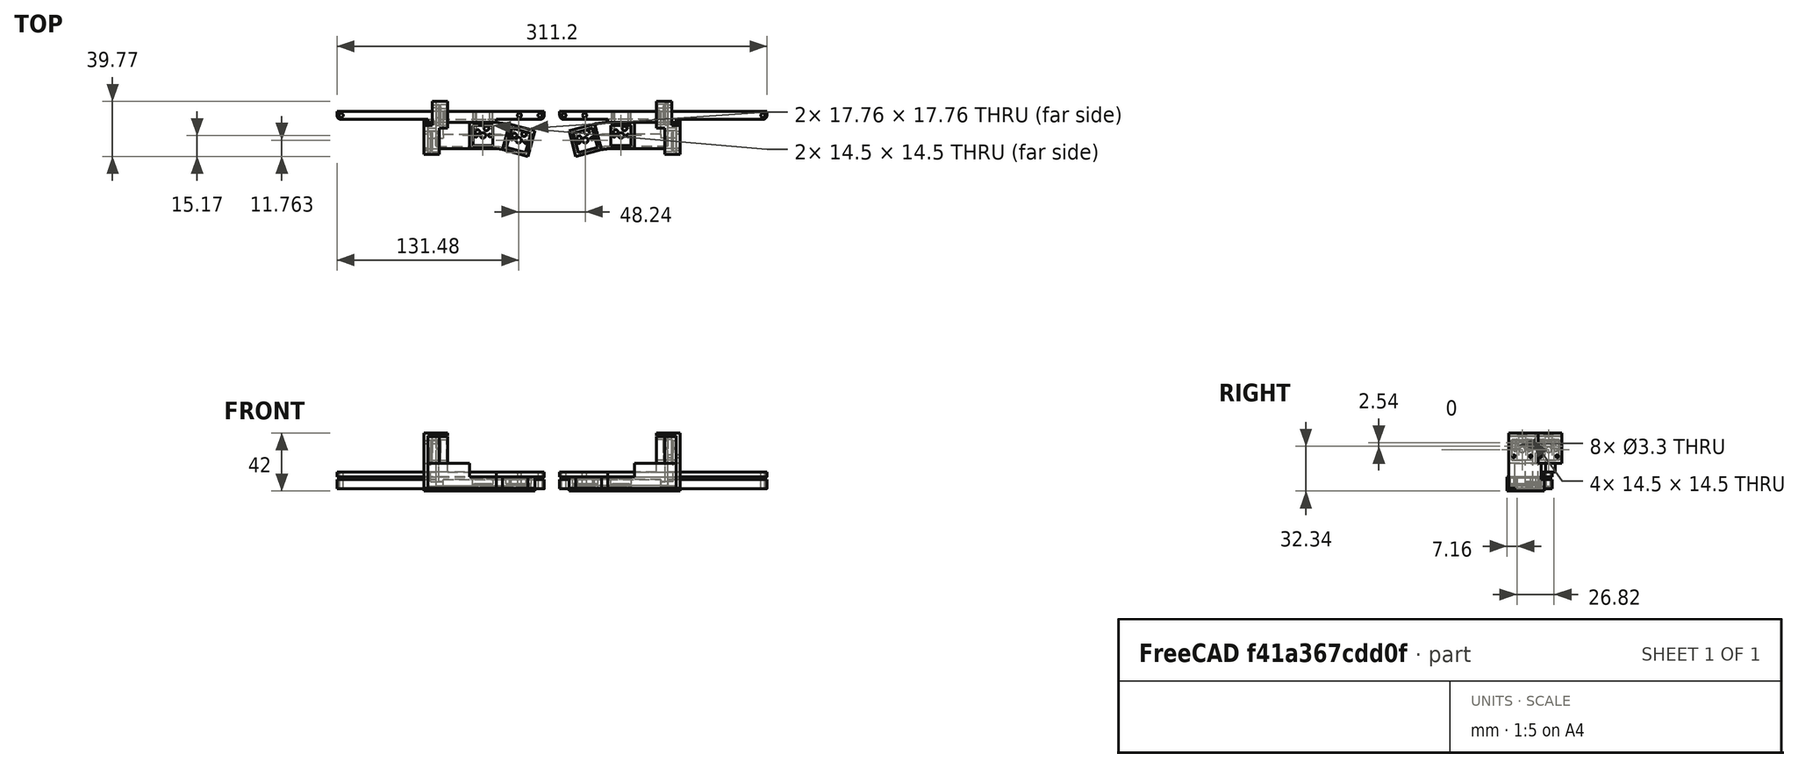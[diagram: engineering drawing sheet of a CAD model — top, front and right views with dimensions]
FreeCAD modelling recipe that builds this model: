
FCSTD DOCUMENT  (FreeCAD 0.21R33771 (Git))
Label: thumb_v2
License: All rights reserved
LicenseURL: https://en.wikipedia.org/wiki/All_rights_reserved
objects: Part::Box×23, Part::FeaturePython×21, Part::MultiFuse×20, Part::Part2DObjectPython×16, Part::Extrusion×16, Part::Cylinder×14, Part::Cut×11, Part::Fillet×2, Spreadsheet::Sheet×1
note: 123 computed .brp shape members not serialized (recipe doc carries the construction recipe); baked Part::Feature solids carry a one-line shape summary decoded from their .brp

FEATURE [Part::Box] Box  label="Cube"
  AttacherType = Attacher::AttachEngine3D
  Height = 8.2
  Length = 19.2
  Placement = pos=(-9.6,-9.6,-3.2) rot=(0,0,1;0rad)
  Width = 19.2
  expr: .Placement.Base.x = -<<CMX_Socket>>.s1 / 2
  expr: .Placement.Base.y = -<<CMX_Socket>>.s1 / 2
  expr: Length = <<CMX_Socket>>.s1
  expr: Width = <<CMX_Socket>>.s1
FEATURE [Part::Part2DObjectPython] Circle  # Draft 2D object (typed FeaturePython)
  Area = 12.5664
  FirstAngle = 0
  LastAngle = 0
  MakeFace = true
  Radius = 2
  expr: Radius = <<CMX_Socket>>.r1
FEATURE [Part::Part2DObjectPython] Circle001  # Draft 2D object (typed FeaturePython)
  Area = 4.15476
  FirstAngle = 0
  LastAngle = 0
  MakeFace = true
  Placement = pos=(-5.08,-2e-16,0) rot=(0,0,1;0rad)
  Radius = 1.15
  expr: .Placement.Base.x = -<<CMX_Socket>>.xr
  expr: Radius = <<CMX_Socket>>.r3
FEATURE [Part::Part2DObjectPython] Circle002  # Draft 2D object (typed FeaturePython)
  Area = 3.14159
  FirstAngle = 0
  LastAngle = 0
  MakeFace = true
  Placement = pos=(5.08,-2e-16,0) rot=(0,0,1;0rad)
  Radius = 1
  expr: .Placement.Base.x = <<CMX_Socket>>.xr
FEATURE [Part::Part2DObjectPython] Circle003  # Draft 2D object (typed FeaturePython)
  Area = 8.55299
  FirstAngle = 0
  LastAngle = 0
  MakeFace = true
  Placement = pos=(2.54,5.08,0) rot=(0,0,1;0rad)
  Radius = 1.65
  expr: .Placement.Base.x = <<CMX_Socket>>.x1
  expr: .Placement.Base.y = <<CMX_Socket>>.y1
  expr: Radius = <<CMX_Socket>>.r2
FEATURE [Part::Part2DObjectPython] Circle004  # Draft 2D object (typed FeaturePython)
  Area = 8.55299
  FirstAngle = 0
  LastAngle = 0
  MakeFace = true
  Placement = pos=(-3.81,2.54,0) rot=(0,0,1;0rad)
  Radius = 1.65
  expr: .Placement.Base.x = <<CMX_Socket>>.x2
  expr: .Placement.Base.y = <<CMX_Socket>>.y2
  expr: Radius = <<CMX_Socket>>.r2
FEATURE [Part::Extrusion] Extrude002
  Base = -> Circle
  Dir = (0,0,1)
  DirMode = 2
  FaceMakerClass = Part::FaceMakerBullseye
  LengthFwd = -3.2
  LengthRev = 0
  Solid = false
  Symmetric = false
  expr: LengthFwd = -<<CMX_Socket>>.h1 - <<CMX_Socket>>.h2
FEATURE [Part::Extrusion] Extrude003
  Base = -> Circle001
  Dir = (0,0,1)
  DirMode = 2
  FaceMakerClass = Part::FaceMakerBullseye
  LengthFwd = -3.2
  LengthRev = 0
  Solid = false
  Symmetric = false
  expr: LengthFwd = -<<CMX_Socket>>.h1 - <<CMX_Socket>>.h2
FEATURE [Part::Extrusion] Extrude004
  Base = -> Circle002
  Dir = (0,0,1)
  DirMode = 2
  FaceMakerClass = Part::FaceMakerBullseye
  LengthFwd = -3.2
  LengthRev = 0
  Solid = false
  Symmetric = false
  expr: LengthFwd = -<<CMX_Socket>>.h1 - <<CMX_Socket>>.h2
FEATURE [Part::Extrusion] Extrude005
  Base = -> Circle003
  Dir = (0,0,1)
  DirMode = 2
  FaceMakerClass = Part::FaceMakerBullseye
  LengthFwd = -1
  LengthRev = 0
  Solid = false
  Symmetric = false
  expr: LengthFwd = -<<CMX_Socket>>.h2
FEATURE [Part::Extrusion] Extrude006
  Base = -> Circle004
  Dir = (0,0,1)
  DirMode = 2
  FaceMakerClass = Part::FaceMakerBullseye
  LengthFwd = -1
  LengthRev = 0
  Solid = false
  Symmetric = false
  expr: LengthFwd = -<<CMX_Socket>>.h2
FEATURE [Part::Part2DObjectPython] Rectangle  # Draft 2D object (typed FeaturePython)
  Area = 90.6
  ChamferSize = 0
  Columns = 1
  FilletRadius = 0
  Height = 6
  Length = 15.1
  MakeFace = true
  Placement = pos=(-8.03,0.8,-1) rot=(0,0,1;0rad)
  Rows = 1
  expr: .Placement.Base.x = <<CMX_Socket>>.xl
  expr: .Placement.Base.y = <<CMX_Socket>>.yl
  expr: .Placement.Base.z = -<<CMX_Socket>>.h2
  expr: Height = <<CMX_Socket>>.ll
  expr: Length = <<CMX_Socket>>.wl
FEATURE [Part::Extrusion] Extrude007
  Base = -> Rectangle
  Dir = (0,0,1)
  DirMode = 2
  FaceMakerClass = Part::FaceMakerBullseye
  LengthFwd = -2.2
  LengthRev = 0
  Solid = false
  Symmetric = false
  expr: LengthFwd = -<<CMX_Socket>>.h1
FEATURE [Part::Part2DObjectPython] Rectangle001  # Draft 2D object (typed FeaturePython)
  Area = 225
  ChamferSize = 0
  Columns = 1
  FilletRadius = 0
  Height = 15
  Length = 15
  MakeFace = true
  Placement = pos=(-7.5,-7.5,0) rot=(0,0,1;0rad)
  Rows = 1
  expr: .Placement.Base.x = -<<CMX_Socket>>.s2 / 2
  expr: .Placement.Base.y = -<<CMX_Socket>>.s2 / 2
  expr: Height = <<CMX_Socket>>.s2
  expr: Length = <<CMX_Socket>>.s2
FEATURE [Part::Extrusion] Extrude001
  Base = -> Rectangle001
  Dir = (0,0,1)
  DirMode = 2
  FaceMakerClass = Part::FaceMakerBullseye
  LengthFwd = 4.5
  LengthRev = 0
  Solid = false
  Symmetric = false
  expr: LengthFwd = <<CMX_Socket>>.h3
FEATURE [Part::Part2DObjectPython] Rectangle002  # Draft 2D object (typed FeaturePython)
  Area = 210.25
  ChamferSize = 0
  Columns = 1
  FilletRadius = 0
  Height = 14.5
  Length = 14.5
  MakeFace = true
  Placement = pos=(-7.25,-7.25,4) rot=(0,0,1;0rad)
  Rows = 1
  expr: .Placement.Base.x = -<<CMX_Socket>>.s3 / 2
  expr: .Placement.Base.y = -<<CMX_Socket>>.s3 / 2
  expr: Height = <<CMX_Socket>>.s3
  expr: Length = <<CMX_Socket>>.s3
FEATURE [Part::Extrusion] Extrude
  Base = -> Rectangle002
  Dir = (0,0,1)
  DirMode = 2
  FaceMakerClass = Part::FaceMakerBullseye
  LengthFwd = 1.1
  LengthRev = 0
  Solid = false
  Symmetric = false
FEATURE [Part::MultiFuse] Fusion
  Shapes = -> [Extrude001,Extrude002,Extrude003,Extrude004,Extrude005,Extrude006,Extrude007,Extrude]
FEATURE [Part::Cut] Cut
  Base = -> Box
  Tool = -> Fusion
FEATURE [Spreadsheet::Sheet] Spreadsheet  label="CMX_Socket"
  cells = B3='r1; C3(r1)=2; D3='x1; E3(x1)=2.54; F3='y1; G3(y1)=5.08; B4='r2; C4(r2)=1.65; D4='x2; E4(x2)=-3.81; F4='y2; G4(y2)=2.54; B5='r3; C5(r3)=1.15; D5='xr; E5(xr)=5.08; B7='wl; C7(wl)=15.1; D7='xl; E7(xl)=-8.03; B8='ll; C8(ll)=6; D8='yl; E8(yl)=0.8; B10='h1; C10(h1)=2.2; B11='h2; C11(h2)=1; B12='h3; C12(h3)=4.5; B14='s1; C14(s1)=19.2; B15='s2; C15(s2)=15; B16='s3; C16(s3)=14.5
FEATURE [Part::FeaturePython] Clone  label="Cut001"  # Draft clone (typed FeaturePython)
  AttacherType = Attacher::AttachEngine3D
  Fuse = false
  Objects = -> [Cut]
  Placement = pos=(-30.6,15,24.6) rot=(0.57735,0.57735,0.57735;2.0944rad)
  Scale = (1,1,1)
FEATURE [Part::FeaturePython] Clone001  label="Cut002"  # Draft clone (typed FeaturePython)
  AttacherType = Attacher::AttachEngine3D
  Fuse = false
  Objects = -> [Clone]
  Placement = pos=(-36.6,-4.2,24.6) rot=(0.57735,0.57735,0.57735;2.0944rad)
  Scale = (1,1,1)
FEATURE [Part::FeaturePython] Clone002  label="Cut003"  # Draft clone (typed FeaturePython)
  AttacherType = Attacher::AttachEngine3D
  Fuse = false
  Objects = -> [Clone001]
  Scale = (1,1,1)
FEATURE [Part::FeaturePython] Clone003  label="Cut004"  # Draft clone (typed FeaturePython)
  AttacherType = Attacher::AttachEngine3D
  Fuse = false
  Objects = -> [Clone002]
  Placement = pos=(25.88,-3.407,0) rot=(0,0,-1;0.261799rad)
  Scale = (1,1,1)
FEATURE [Part::Part2DObjectPython] Rectangle003  # Draft 2D object (typed FeaturePython)
  Area = 900
  ChamferSize = 0
  Columns = 1
  FilletRadius = 0
  Height = 6
  Length = 150
  MakeFace = true
  Placement = pos=(-120.6,9.6,5) rot=(0,0,1;0rad)
  Rows = 1
FEATURE [Part::Extrusion] Extrude008
  Base = -> Rectangle003
  Dir = (0,0,1)
  DirMode = 2
  FaceMakerClass = Part::FaceMakerBullseye
  LengthFwd = 3.4
  LengthRev = 0
  Solid = false
  Symmetric = false
FEATURE [Part::Fillet] Fillet
  Base = -> Extrude008
  Edges = 2 edges r=3: [Edge1,Edge2]
FEATURE [Part::Part2DObjectPython] Wire  # Draft 2D object (typed FeaturePython)
  Area = 134.571
  ChamferSize = 0
  Closed = true
  End = (9.6,9.6,0)
  FilletRadius = 0
  Length = 52.5388
  MakeFace = true
  Placement = pos=(9.59644,-9.60026,0) rot=(0,0,1;0rad)
  Points = (4) [(0,0,0),(4.52594,-0.594952,0),(9.49533,17.9508,0),(0.00355721,19.2003,0)]
  Start = (9.59644,-9.60026,0)
  Subdivisions = 0
FEATURE [Part::Extrusion] Extrude009
  Base = -> Wire
  Dir = (0,0,1)
  DirMode = 2
  FaceMakerClass = Part::FaceMakerBullseye
  LengthFwd = 8.2
  LengthRev = 0
  Placement = pos=(0,0,-3.2) rot=(0,0,1;0rad)
  Solid = false
  Symmetric = false
FEATURE [Part::Part2DObjectPython] Rectangle004  # Draft 2D object (typed FeaturePython)
  Area = 579.84
  ChamferSize = 0
  Columns = 1
  FilletRadius = 0
  Height = 19.2
  Length = 30.2
  MakeFace = true
  Placement = pos=(-39.8,-9.6,-3.2) rot=(0,0,1;0rad)
  Rows = 1
FEATURE [Part::Extrusion] Extrude010
  Base = -> Rectangle004
  Dir = (0,0,1)
  DirMode = 2
  FaceMakerClass = Part::FaceMakerBullseye
  LengthFwd = 18.2
  LengthRev = 0
  Solid = false
  Symmetric = false
FEATURE [Part::Cylinder] Cylinder
  Angle = 360
  AttacherType = Attacher::AttachEngine3D
  FirstAngle = 0
  Height = 10
  Placement = pos=(-117.6,12.6,0) rot=(0,0,1;0rad)
  Radius = 1.5
  SecondAngle = 0
FEATURE [Part::Cylinder] Cylinder001
  Angle = 360
  AttacherType = Attacher::AttachEngine3D
  FirstAngle = 0
  Height = 10
  Placement = pos=(26.4,12.6,0) rot=(0,0,1;0rad)
  Radius = 1.5
  SecondAngle = 0
FEATURE [Part::Cylinder] Cylinder002
  Angle = 360
  AttacherType = Attacher::AttachEngine3D
  FirstAngle = 0
  Height = 10
  Placement = pos=(11.4,12.6,0) rot=(0,0,1;0rad)
  Radius = 1.5
  SecondAngle = 0
FEATURE [Part::Part2DObjectPython] Rectangle005  # Draft 2D object (typed FeaturePython)
  Area = 82
  ChamferSize = 0
  Columns = 1
  FilletRadius = 0
  Height = 10
  Length = 8.2
  MakeFace = true
  Placement = pos=(-33.8,9.6,8.4) rot=(0,0,1;0rad)
  Rows = 1
FEATURE [Part::Extrusion] Extrude011
  Base = -> Rectangle005
  Dir = (0,0,1)
  DirMode = 2
  FaceMakerClass = Part::FaceMakerBullseye
  LengthFwd = 8
  LengthRev = 0
  Solid = false
  Symmetric = false
FEATURE [Part::MultiFuse] Fusion001
  Shapes = -> [Cylinder,Cylinder001,Cylinder002]
FEATURE [Part::Cut] Cut001  label="Cut005"
  Base = -> Fillet
  Placement = pos=(15,2,0) rot=(0,0,1;0rad)
  Tool = -> Fusion001
FEATURE [Part::MultiFuse] Fusion002
  Shapes = -> [Clone002,Clone003,Extrude009]
FEATURE [Part::MultiFuse] Fusion003
  Shapes = -> [Clone,Clone001,Extrude010,Extrude011]
FEATURE [Part::FeaturePython] Clone004  label="Cut006"  # Draft clone (typed FeaturePython)
  AttacherType = Attacher::AttachEngine3D
  Fuse = false
  Objects = -> [Cut001]
  Placement = pos=(85,2,0) rot=(0,0,1;0rad)
  Scale = (-1,1,1)
FEATURE [Part::FeaturePython] Clone005  label="clone"  # Draft clone (typed FeaturePython)
  AttacherType = Attacher::AttachEngine3D
  Fuse = false
  Objects = -> [Extrude009]
  Placement = pos=(100.001,0,-3.2) rot=(0,0,1;0rad)
  Scale = (-1,1,1)
FEATURE [Part::FeaturePython] Clone006  label="Extrude012"  # Draft clone (typed FeaturePython)
  AttacherType = Attacher::AttachEngine3D
  Fuse = false
  Objects = -> [Extrude010]
  Placement = pos=(100,0,0) rot=(0,0,1;0rad)
  Scale = (-1,1,1)
FEATURE [Part::FeaturePython] Clone007  label="Extrude013"  # Draft clone (typed FeaturePython)
  AttacherType = Attacher::AttachEngine3D
  Fuse = false
  Objects = -> [Extrude011]
  Placement = pos=(100,0,0) rot=(0,0,1;0rad)
  Scale = (-1,1,1)
FEATURE [Part::FeaturePython] Clone008  label="Cut007"  # Draft clone (typed FeaturePython)
  AttacherType = Attacher::AttachEngine3D
  Fuse = false
  Objects = -> [Cut]
  Placement = pos=(130.6,15,24.6) rot=(0.57735,-0.57735,-0.57735;2.0944rad)
  Scale = (1,1,1)
FEATURE [Part::FeaturePython] Clone009  label="Cut008"  # Draft clone (typed FeaturePython)
  AttacherType = Attacher::AttachEngine3D
  Fuse = false
  Objects = -> [Clone008]
  Placement = pos=(136.6,-4.2,24.6) rot=(0.57735,-0.57735,-0.57735;2.0944rad)
  Scale = (1,1,1)
FEATURE [Part::FeaturePython] Clone010  label="Cut009"  # Draft clone (typed FeaturePython)
  AttacherType = Attacher::AttachEngine3D
  Fuse = false
  Objects = -> [Cut]
  Placement = pos=(100,0,0) rot=(0,0,1;0rad)
  Scale = (1,1,1)
FEATURE [Part::FeaturePython] Clone011  label="Cut010"  # Draft clone (typed FeaturePython)
  AttacherType = Attacher::AttachEngine3D
  Fuse = false
  Objects = -> [Clone010]
  Placement = pos=(74.12,-3.41,0) rot=(0,0,1;0.261799rad)
  Scale = (1,1,1)
FEATURE [Part::Box] Box001  label="Cube001"
  AttacherType = Attacher::AttachEngine3D
  Height = 19.8
  Length = 3
  Placement = pos=(-36.8,5.4,14.4) rot=(0,0,1;0rad)
  Width = 19.2
FEATURE [Part::Box] Box002  label="Cube002"
  AttacherType = Attacher::AttachEngine3D
  Height = 1
  Length = 1
  Placement = pos=(-32.8,12,34.2) rot=(0,0,1;0rad)
  Width = 6
FEATURE [Part::Box] Box003  label="Cube003"
  AttacherType = Attacher::AttachEngine3D
  Height = 2
  Length = 11.2
  Placement = pos=(-36.8,5.4,34.2) rot=(0,0,1;0rad)
  Width = 19.2
FEATURE [Part::Box] Box004  label="Cube004"
  AttacherType = Attacher::AttachEngine3D
  Height = 1.15
  Length = 1.3
  Placement = pos=(-28.05,11.85,34.2) rot=(0,0,1;0rad)
  Width = 6.3
FEATURE [Part::Cut] Cut002  label="Cut011"
  Base = -> Box003
  Tool = -> Box004
FEATURE [Part::Box] Box005  label="Cube005"
  AttacherType = Attacher::AttachEngine3D
  Height = 1
  Length = 1
  Placement = pos=(-38.8,-7.2,34.2) rot=(0,0,1;0rad)
  Width = 6
FEATURE [Part::MultiFuse] Fusion006
  Placement = pos=(0,0,0.6) rot=(0,0,1;0rad)
  Shapes = -> [Box001,Cut002]
FEATURE [Part::Box] Box006  label="Cube006"
  AttacherType = Attacher::AttachEngine3D
  Height = 38
  Length = 3
  Placement = pos=(-36.8,5.4,-3.8) rot=(0,0,1;0rad)
  Width = 19.2
FEATURE [Part::Box] Box007  label="Cube007"
  AttacherType = Attacher::AttachEngine3D
  Height = 2
  Length = 11.2
  Placement = pos=(-36.8,5.4,34.2) rot=(0,0,1;0rad)
  Width = 19.2
FEATURE [Part::Box] Box008  label="Cube008"
  AttacherType = Attacher::AttachEngine3D
  Height = 1.15
  Length = 1.3
  Placement = pos=(-28.05,11.85,34.2) rot=(0,0,1;0rad)
  Width = 6.3
FEATURE [Part::Cut] Cut003  label="Cut012"
  Base = -> Box007
  Tool = -> Box008
FEATURE [Part::MultiFuse] Fusion007
  Placement = pos=(-6,-19.2,0.6) rot=(0,0,1;0rad)
  Shapes = -> [Box006,Cut003]
FEATURE [Part::Box] Box009  label="Cube009"
  AttacherType = Attacher::AttachEngine3D
  Height = 21.8
  Length = 6
  Placement = pos=(-42.8,5.4,15) rot=(0,0,1;0rad)
  Width = 2
FEATURE [Part::Box] Box010  label="Cube010"
  AttacherType = Attacher::AttachEngine3D
  Height = 2
  Length = 52.4
  Placement = pos=(-42.8,-9.6,-5.2) rot=(0,0,1;0rad)
  Width = 19.2
FEATURE [Part::Part2DObjectPython] Wire001  # Draft 2D object (typed FeaturePython)
  Area = 134.571
  ChamferSize = 0
  Closed = true
  End = (9.6,9.6,0)
  FilletRadius = 0
  Length = 52.5388
  MakeFace = true
  Placement = pos=(9.59644,-9.60026,0) rot=(0,0,1;0rad)
  Points = (4) [(0,0,0),(4.52594,-0.594952,0),(9.49533,17.9508,0),(0.00355721,19.2003,0)]
  Start = (9.59644,-9.60026,0)
  Subdivisions = 0
FEATURE [Part::Extrusion] Extrude012
  Base = -> Wire001
  Dir = (0,0,1)
  DirMode = 2
  FaceMakerClass = Part::FaceMakerBullseye
  LengthFwd = 2
  LengthRev = 0
  Placement = pos=(0,0,-5.2) rot=(0,0,1;0rad)
  Solid = false
  Symmetric = false
FEATURE [Part::Part2DObjectPython] Rectangle006  # Draft 2D object (typed FeaturePython)
  Area = 368.64
  ChamferSize = 0
  Columns = 1
  FilletRadius = 0
  Height = 19.2
  Length = 19.2
  MakeFace = true
  Placement = pos=(-9.6,9.6,-5.2) rot=(1,0,0;3.14159rad)
  Rows = 1
FEATURE [Part::Extrusion] Extrude013  label="Extrude014"
  Base = -> Rectangle006
  Dir = (0,-1e-16,-1)
  DirMode = 2
  FaceMakerClass = Part::FaceMakerBullseye
  LengthFwd = 0
  LengthRev = 2
  Placement = pos=(25.88,-3.41,0) rot=(0,0,-1;0.261799rad)
  Solid = false
  Symmetric = false
FEATURE [Part::Cylinder] Cylinder003
  Angle = 360
  AttacherType = Attacher::AttachEngine3D
  FirstAngle = 0
  Height = 10
  Placement = pos=(-117.6,12.6,5) rot=(0,0,1;0rad)
  Radius = 1.5
  SecondAngle = 0
FEATURE [Part::Cylinder] Cylinder004
  Angle = 360
  AttacherType = Attacher::AttachEngine3D
  FirstAngle = 0
  Height = 10
  Placement = pos=(26.4,12.6,5) rot=(0,0,1;0rad)
  Radius = 1.5
  SecondAngle = 0
FEATURE [Part::Cylinder] Cylinder005
  Angle = 360
  AttacherType = Attacher::AttachEngine3D
  FirstAngle = 0
  Height = 10
  Placement = pos=(11.4,12.6,5) rot=(0,0,1;0rad)
  Radius = 1.5
  SecondAngle = 0
FEATURE [Part::MultiFuse] Fusion008
  Shapes = -> [Cylinder003,Cylinder004,Cylinder005]
FEATURE [Part::Part2DObjectPython] Rectangle007  # Draft 2D object (typed FeaturePython)
  Area = 900
  ChamferSize = 0
  Columns = 1
  FilletRadius = 0
  Height = 6
  Length = 150
  MakeFace = true
  Placement = pos=(-120.6,9.6,5) rot=(0,0,1;0rad)
  Rows = 1
FEATURE [Part::Extrusion] Extrude014  label="Extrude015"
  Base = -> Rectangle007
  Dir = (0,0,1)
  DirMode = 2
  FaceMakerClass = Part::FaceMakerBullseye
  LengthFwd = 6.6
  LengthRev = 0
  Solid = false
  Symmetric = false
FEATURE [Part::Fillet] Fillet001
  Base = -> Extrude014
  Edges = 2 edges r=3: [Edge1,Edge2]
FEATURE [Part::Cut] Cut004  label="Cut013"
  Base = -> Fillet001
  Placement = pos=(15,2,-8.6) rot=(0,0,1;0rad)
  Tool = -> Fusion008
FEATURE [Part::FeaturePython] Clone012  label="Cube011"  # Draft clone (typed FeaturePython)
  AttacherType = Attacher::AttachEngine3D
  Fuse = false
  Objects = -> [Box002]
  Placement = pos=(127.9,12,34.2) rot=(0,0,1;0rad)
  Scale = (-1,1,1)
FEATURE [Part::FeaturePython] Clone013  label="Cube012"  # Draft clone (typed FeaturePython)
  AttacherType = Attacher::AttachEngine3D
  Fuse = false
  Objects = -> [Box005]
  Placement = pos=(133.9,-7.2,34.2) rot=(0,0,1;0rad)
  Scale = (-1,1,1)
FEATURE [Part::MultiFuse] Fusion010  label="Fusion011"
  Placement = pos=(4.9,0,0) rot=(0,0,1;0rad)
  Shapes = -> [Box002,Box005]
FEATURE [Part::MultiFuse] Fusion013  label="Fusion014"
  Shapes = -> [Box010,Extrude012,Extrude013]
FEATURE [Part::Box] Box011  label="Cube013"
  AttacherType = Attacher::AttachEngine3D
  Height = 8.2
  Length = 52.4
  Placement = pos=(-42.8,9.6,-5.2) rot=(0,0,1;0rad)
  Width = 2
FEATURE [Part::Box] Box012  label="Cube014"
  AttacherType = Attacher::AttachEngine3D
  Height = 3.4
  Length = 49.4
  Placement = pos=(90.4,9.6,5) rot=(0,0,1;0rad)
  Width = 2
FEATURE [Part::MultiFuse] Fusion015  label="Fusion017"
  Shapes = -> [Clone005,Clone010,Clone011]
FEATURE [Part::MultiFuse] Fusion016  label="Fusion018"
  Shapes = -> [Clone005,Clone010,Clone011,Clone004,Clone006,Clone008,Clone009,Clone012,Clone013,Clone007,Box012,Fusion015]
FEATURE [Part::Box] Box013  label="Cube015"
  AttacherType = Attacher::AttachEngine3D
  Height = 3.4
  Length = 49.4
  Placement = pos=(-39.8,9.6,5) rot=(0,0,1;0rad)
  Width = 2
FEATURE [Part::MultiFuse] Fusion017  label="Fusion019"
  Shapes = -> [Cut001,Fusion002,Fusion003,Fusion010,Box013]
FEATURE [Part::Cylinder] Cylinder006
  Angle = 360
  AttacherType = Attacher::AttachEngine3D
  FirstAngle = 0
  Height = 20
  Placement = pos=(6,25,-3.2) rot=(1,0,0;1.5708rad)
  Radius = 1
  SecondAngle = 0
FEATURE [Part::Cylinder] Cylinder007
  Angle = 360
  AttacherType = Attacher::AttachEngine3D
  FirstAngle = 0
  Height = 20
  Placement = pos=(-6,25,-3.2) rot=(1,0,0;1.5708rad)
  Radius = 1
  SecondAngle = 0
FEATURE [Part::MultiFuse] Fusion018  label="Fusion020"
  Shapes = -> [Cylinder006,Cylinder007]
FEATURE [Part::Cylinder] Cylinder008
  Angle = 360
  AttacherType = Attacher::AttachEngine3D
  FirstAngle = 0
  Height = 7
  Placement = pos=(6,12,-3.2) rot=(1,0,0;1.5708rad)
  Radius = 1
  SecondAngle = 0
FEATURE [Part::Cylinder] Cylinder009
  Angle = 360
  AttacherType = Attacher::AttachEngine3D
  FirstAngle = 0
  Height = 7
  Placement = pos=(-6,12,-3.2) rot=(1,0,0;1.5708rad)
  Radius = 1
  SecondAngle = 0
FEATURE [Part::MultiFuse] Fusion019  label="Fusion021"
  Placement = pos=(25.88,-3.41,0) rot=(0,0,-1;0.261799rad)
  Shapes = -> [Cylinder008,Cylinder009]
FEATURE [Part::Cylinder] Cylinder010
  Angle = 360
  AttacherType = Attacher::AttachEngine3D
  FirstAngle = 0
  Height = 10
  Placement = pos=(0,6,0) rot=(0,1,0;1.5708rad)
  Radius = 1
  SecondAngle = 0
FEATURE [Part::Cylinder] Cylinder011
  Angle = 360
  AttacherType = Attacher::AttachEngine3D
  FirstAngle = 0
  Height = 10
  Placement = pos=(0,-6,0) rot=(0,1,0;1.5708rad)
  Radius = 1
  SecondAngle = 0
FEATURE [Part::MultiFuse] Fusion020  label="Fusion022"
  Placement = pos=(-40,15,30) rot=(0,0,1;0rad)
  Shapes = -> [Cylinder010,Cylinder011]
FEATURE [Part::Cylinder] Cylinder012
  Angle = 360
  AttacherType = Attacher::AttachEngine3D
  FirstAngle = 0
  Height = 10
  Placement = pos=(0,6,0) rot=(0,1,0;1.5708rad)
  Radius = 1
  SecondAngle = 0
FEATURE [Part::Cylinder] Cylinder013
  Angle = 360
  AttacherType = Attacher::AttachEngine3D
  FirstAngle = 0
  Height = 10
  Placement = pos=(0,-6,0) rot=(0,1,0;1.5708rad)
  Radius = 1
  SecondAngle = 0
FEATURE [Part::MultiFuse] Fusion021  label="Fusion023"
  Placement = pos=(-48,-4.2,30) rot=(0,0,1;0rad)
  Shapes = -> [Cylinder012,Cylinder013]
FEATURE [Part::MultiFuse] Fusion022  label="Fusion024"
  Shapes = -> [Fusion018,Fusion019,Fusion020,Fusion021]
FEATURE [Part::FeaturePython] Clone015  label="Fusion026"  # Draft clone (typed FeaturePython)
  AttacherType = Attacher::AttachEngine3D
  Fuse = false
  Objects = -> [Fusion018]
  Placement = pos=(100,0,0) rot=(0,0,1;0rad)
  Scale = (-1,1,1)
FEATURE [Part::FeaturePython] Clone016  label="Fusion027"  # Draft clone (typed FeaturePython)
  AttacherType = Attacher::AttachEngine3D
  Fuse = false
  Objects = -> [Fusion019]
  Placement = pos=(74.12,-3.41,0) rot=(0,0,1;0.261799rad)
  Scale = (1,1,1)
FEATURE [Part::FeaturePython] Clone017  label="Fusion028"  # Draft clone (typed FeaturePython)
  AttacherType = Attacher::AttachEngine3D
  Fuse = false
  Objects = -> [Fusion020]
  Placement = pos=(130,15,20) rot=(0,0,1;0rad)
  Scale = (1,1,1)
FEATURE [Part::FeaturePython] Clone018  label="Fusion029"  # Draft clone (typed FeaturePython)
  AttacherType = Attacher::AttachEngine3D
  Fuse = false
  Objects = -> [Fusion021]
  Placement = pos=(138,-4.2,20) rot=(0,0,1;0rad)
  Scale = (1,1,1)
FEATURE [Part::MultiFuse] Fusion023  label="Fusion030"
  Shapes = -> [Clone015,Clone016,Clone017,Clone018]
FEATURE [Part::Box] Box014  label="Cube016"
  AttacherType = Attacher::AttachEngine3D
  Height = 18.2
  Length = 3
  Placement = pos=(-42.8,5.4,-3.2) rot=(0,0,1;0rad)
  Width = 4.2
FEATURE [Part::MultiFuse] Fusion024  label="Fusion031"
  Shapes = -> [Box014,Box011,Fusion013,Cut004,Box009,Fusion007,Fusion006]
FEATURE [Part::FeaturePython] Clone019  label="Fusion032"  # Draft clone (typed FeaturePython)
  AttacherType = Attacher::AttachEngine3D
  Fuse = false
  Objects = -> [Fusion024]
  Placement = pos=(100,0,0) rot=(0,0,1;0rad)
  Scale = (-1,1,1)
FEATURE [Part::Cut] Cut005  label="Cut014"
  Base = -> Fusion024
  Tool = -> Fusion022
FEATURE [Part::Cut] Cut006  label="Cut015"
  Base = -> Clone019
  Tool = -> Fusion023
FEATURE [Part::Part2DObjectPython] Rectangle008  # Draft 2D object (typed FeaturePython)
  Area = 50
  ChamferSize = 0
  Columns = 1
  FilletRadius = 0
  Height = 10
  Length = 5
  MakeFace = true
  Placement = pos=(-33.7,9.6,8.4) rot=(0,0,1;0rad)
  Rows = 1
FEATURE [Part::Extrusion] Extrude015  label="Extrude016"
  Base = -> Rectangle008
  Dir = (0,0,1)
  DirMode = 2
  FaceMakerClass = Part::FaceMakerBullseye
  LengthFwd = 5.4
  LengthRev = 0
  Placement = pos=(0,0,-10) rot=(0,0,1;0rad)
  Solid = false
  Symmetric = false
FEATURE [Part::FeaturePython] Clone020  label="Extrude017"  # Draft clone (typed FeaturePython)
  AttacherType = Attacher::AttachEngine3D
  Fuse = false
  Objects = -> [Extrude015]
  Placement = pos=(162.5,0,-10) rot=(0,0,1;0rad)
  Scale = (1,1,1)
FEATURE [Part::Cut] Cut007  label="Cut016"
  Base = -> Cut006
  Tool = -> Clone020
FEATURE [Part::Cut] Cut008  label="Cut017"
  Base = -> Cut005
  Tool = -> Extrude015
FEATURE [Part::Box] Box015  label="Cube017"
  AttacherType = Attacher::AttachEngine3D
  Height = 9
  Length = 2
  Placement = pos=(-33.8,7.4,17) rot=(0,0,1;0rad)
  Width = 15.2
FEATURE [Part::Box] Box016  label="Cube018"
  AttacherType = Attacher::AttachEngine3D
  Height = 9
  Length = 2
  Placement = pos=(-39.8,-11.8,17) rot=(0,0,1;0rad)
  Width = 15.2
FEATURE [Part::Box] Box017  label="Cube019"
  AttacherType = Attacher::AttachEngine3D
  Height = 18.6
  Length = 2
  Placement = pos=(-33.8,7.4,-1.6) rot=(0,0,1;0rad)
  Width = 5.2
FEATURE [Part::Box] Box018  label="Cube020"
  AttacherType = Attacher::AttachEngine3D
  Height = 18.6
  Length = 2
  Placement = pos=(-39.8,-1.8,-1.6) rot=(0,0,1;0rad)
  Width = 5.2
FEATURE [Part::Box] Box019  label="Cube021"
  AttacherType = Attacher::AttachEngine3D
  Height = 4.8
  Length = 5
  Placement = pos=(-33.8,0.4,-3.2) rot=(0,0,1;0rad)
  Width = 10.2
FEATURE [Part::Box] Box020  label="Cube022"
  AttacherType = Attacher::AttachEngine3D
  Height = 3.2
  Length = 11
  Placement = pos=(-39.8,-1.8,-1.6) rot=(0,0,1;0rad)
  Width = 5.2
FEATURE [Part::Box] Box021  label="Cube023"
  AttacherType = Attacher::AttachEngine3D
  Height = 2
  Length = 47
  Placement = pos=(-33.8,-8,-3.2) rot=(0,0,1;0rad)
  Width = 9
FEATURE [Part::Box] Box022  label="Cube024"
  AttacherType = Attacher::AttachEngine3D
  Height = 2
  Length = 20
  Placement = pos=(10.85,-7.7,-3.2) rot=(0,0,-1;0.261799rad)
  Width = 9
FEATURE [Part::MultiFuse] Fusion025
  Shapes = -> [Box015,Box016,Box017,Box018,Box019,Box020,Box021,Box022]
FEATURE [Part::FeaturePython] Clone021  label="Fusion033"  # Draft clone (typed FeaturePython)
  AttacherType = Attacher::AttachEngine3D
  Fuse = false
  Objects = -> [Fusion025]
  Placement = pos=(100,0,0) rot=(0,0,1;0rad)
  Scale = (-1,1,1)
FEATURE [Part::Cut] Cut009  label="Cut018"
  Base = -> Fusion017
  Tool = -> Fusion025
FEATURE [Part::Cut] Cut010  label="Cut019"
  Base = -> Fusion016
  Tool = -> Clone021
